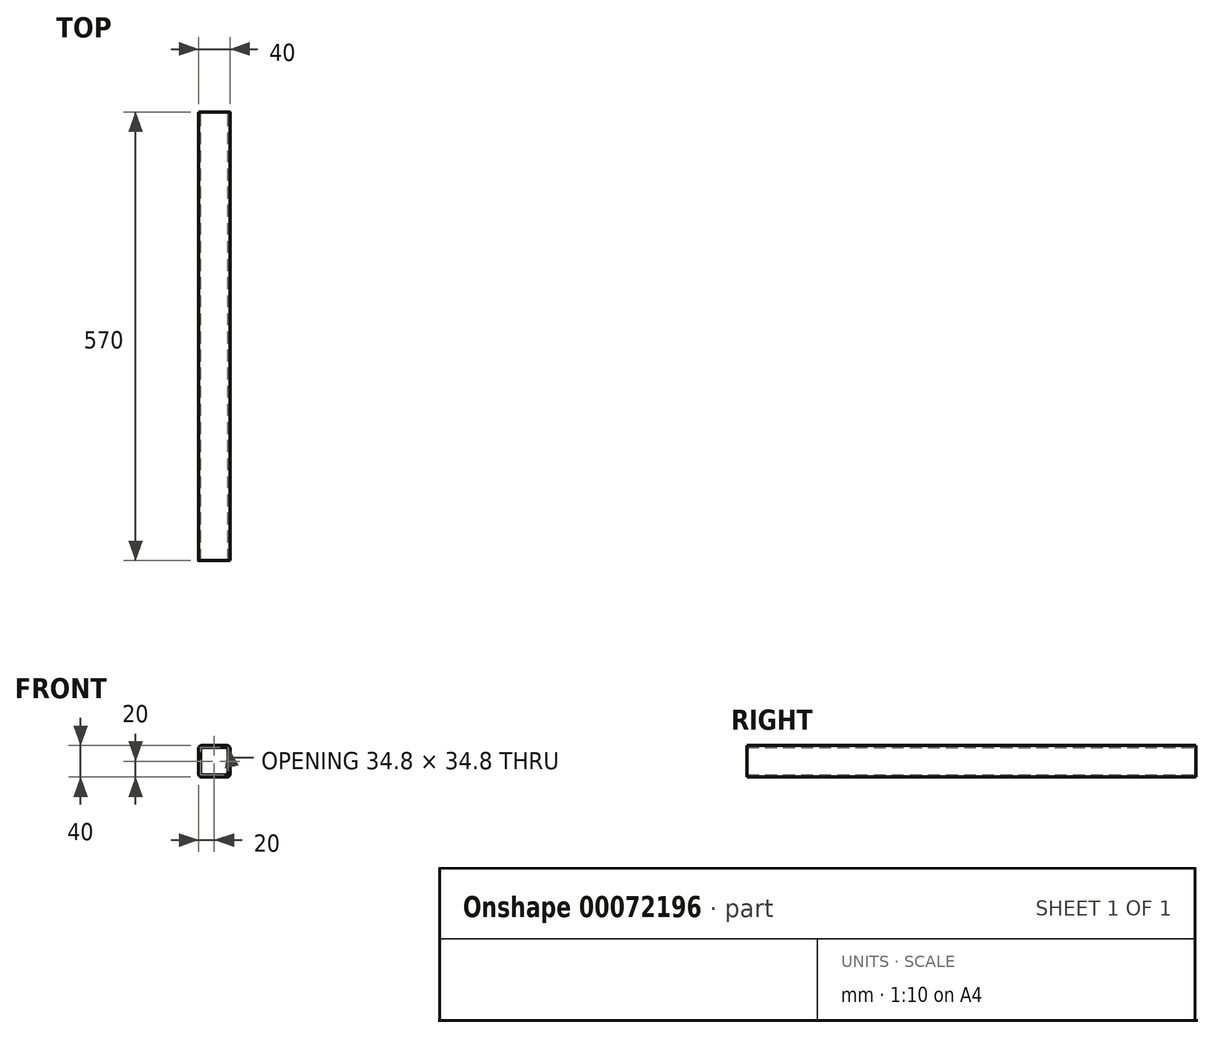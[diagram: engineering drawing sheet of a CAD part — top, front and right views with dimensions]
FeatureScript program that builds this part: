
annotation { "Feature Type Name" : "Feature", "Feature Type Description" : "" }
export const myFeature = defineFeature(function(context is Context, id is Id, definition is map)
    precondition{}
    {
        {
            var Q0;
            Q0=qCreatedBy(makeId("Front.planeOp"),FACE);
            var sketch = newSketch(context, id + "F0", { "sketchPlane" : qUnion([Q0])});
            skLineSegment(sketch, "E0.bottom", {"start": v(-20, 20) * mm, "end": v(20, 20) * mm});
            skLineSegment(sketch, "E0.top", {"start": v(-20, -20) * mm, "end": v(20, -20) * mm});
            skLineSegment(sketch, "E0.left", {"start": v(-20, 20) * mm, "end": v(-20, -20) * mm});
            skLineSegment(sketch, "E0.right", {"start": v(20, 20) * mm, "end": v(20, -20) * mm});
            skLineSegment(sketch, "E1.0", {"start": v(-17.4, 17.4) * mm, "end": v(17.4, 17.4) * mm});
            skLineSegment(sketch, "E1.1", {"start": v(-17.4, 17.4) * mm, "end": v(-17.4, -17.4) * mm});
            skLineSegment(sketch, "E1.2", {"start": v(-17.4, -17.4) * mm, "end": v(17.4, -17.4) * mm});
            skLineSegment(sketch, "E1.3", {"start": v(17.4, 17.4) * mm, "end": v(17.4, -17.4) * mm});
            skSolve(sketch);
        }
        {
            var Q0;
            Q0=makeQuery(id+"F0.imprint","IMPRINT",FACE,{"disambiguationData":[TD([[makeQuery(id+"F0.imprint","IMPRINT",EDGE,{"derivedFrom":sQuery(id+"F0.wireOp",EDGE,"E0.bottom")}),-1.0]])]});
            extrude(context, id + "F1", {"entities" : qUnion([Q0]), "depth" : 570 * mm});
        }
        {
            var Q0;
            Q0=makeQuery(id+"F1.opExtrude","SWEPT_EDGE",EDGE,{"disambiguationData":[OSD([sQuery(id+"F0.wireOp",EDGE,"E1.1"),sQuery(id+"F0.wireOp",EDGE,"E1.2")])]});
            var Q1;
            Q1=makeQuery(id+"F1.opExtrude","SWEPT_EDGE",EDGE,{"disambiguationData":[OSD([sQuery(id+"F0.wireOp",EDGE,"E1.0"),sQuery(id+"F0.wireOp",EDGE,"E1.1")])]});
            var Q2;
            Q2=makeQuery(id+"F1.opExtrude","SWEPT_EDGE",EDGE,{"disambiguationData":[OSD([sQuery(id+"F0.wireOp",EDGE,"E1.0"),sQuery(id+"F0.wireOp",EDGE,"E1.3")])]});
            var Q3;
            Q3=makeQuery(id+"F1.opExtrude","SWEPT_EDGE",EDGE,{"disambiguationData":[OSD([sQuery(id+"F0.wireOp",EDGE,"E1.2"),sQuery(id+"F0.wireOp",EDGE,"E1.3")])]});
            fillet(context, id + "F2", {"entities" : qUnion([Q0, Q1, Q2, Q3]), "radius" : 2 * mm, "tangentPropagation" : true, "allowEdgeOverflow" : false});
        }
        {
            var Q0;
            Q0=makeQuery(id+"F1.opExtrude","SWEPT_EDGE",EDGE,{"disambiguationData":[OSD([sQuery(id+"F0.wireOp",EDGE,"E0.bottom"),sQuery(id+"F0.wireOp",EDGE,"E0.right")])]});
            var Q1;
            Q1=makeQuery(id+"F1.opExtrude","SWEPT_EDGE",EDGE,{"disambiguationData":[OSD([sQuery(id+"F0.wireOp",EDGE,"E0.bottom"),sQuery(id+"F0.wireOp",EDGE,"E0.left")])]});
            var Q2;
            Q2=makeQuery(id+"F1.opExtrude","SWEPT_EDGE",EDGE,{"disambiguationData":[OSD([sQuery(id+"F0.wireOp",EDGE,"E0.top"),sQuery(id+"F0.wireOp",EDGE,"E0.right")])]});
            var Q3;
            Q3=makeQuery(id+"F1.opExtrude","SWEPT_EDGE",EDGE,{"disambiguationData":[OSD([sQuery(id+"F0.wireOp",EDGE,"E0.top"),sQuery(id+"F0.wireOp",EDGE,"E0.left")])]});
            fillet(context, id + "F3", {"entities" : qUnion([Q0, Q1, Q2, Q3]), "radius" : 4 * mm, "tangentPropagation" : true, "allowEdgeOverflow" : false});
        }
    });
